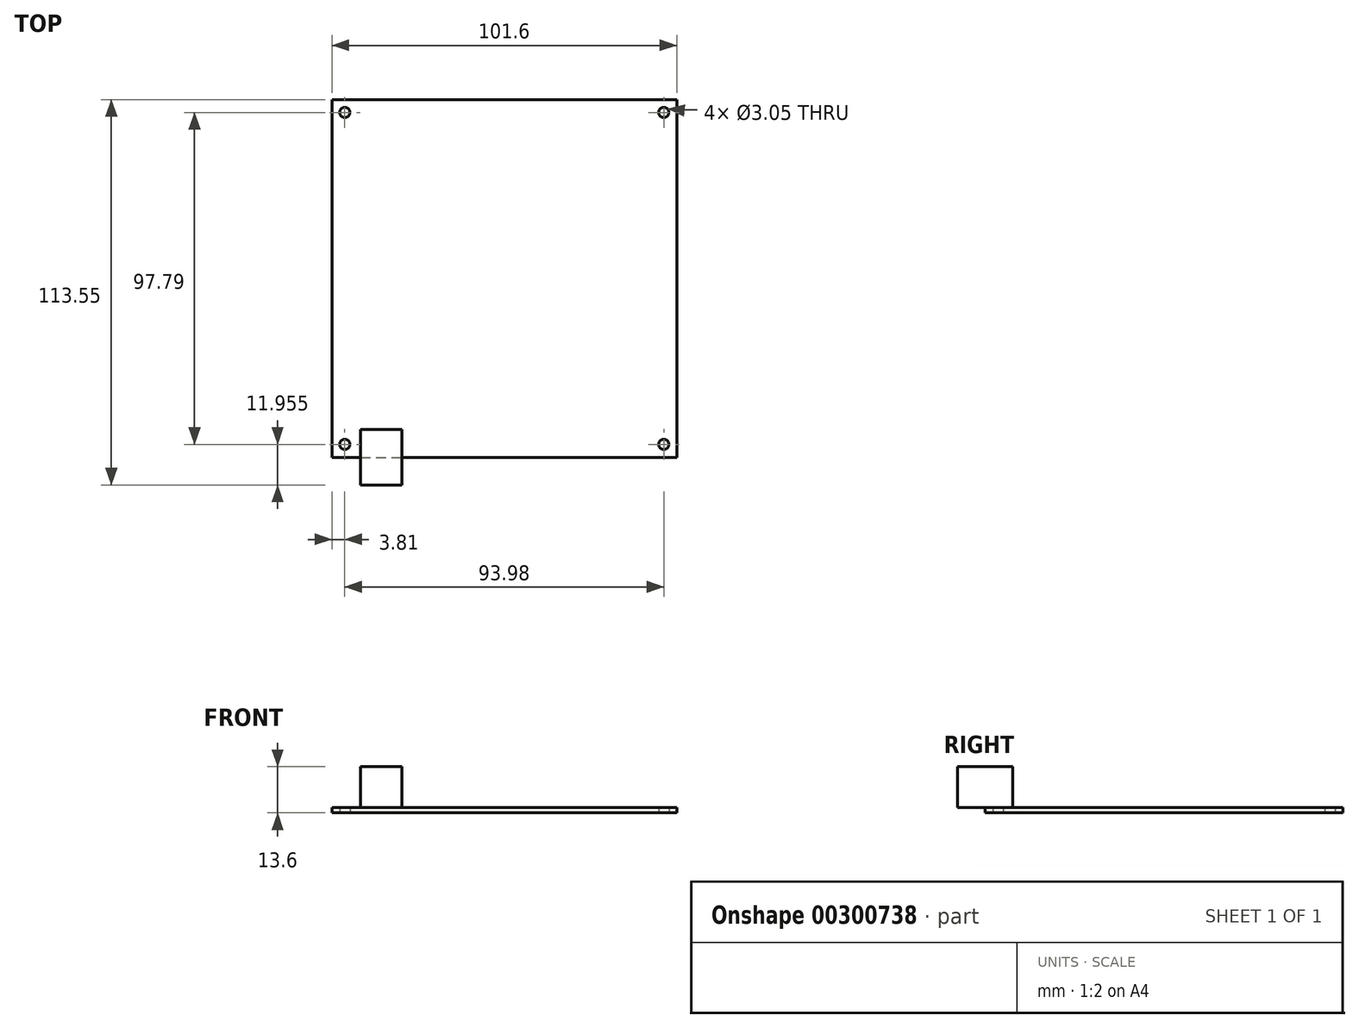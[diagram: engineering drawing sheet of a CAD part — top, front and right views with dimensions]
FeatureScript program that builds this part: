
annotation { "Feature Type Name" : "Feature", "Feature Type Description" : "" }
export const myFeature = defineFeature(function(context is Context, id is Id, definition is map)
    precondition{}
    {
        {
            var Q0;
            Q0=qCreatedBy(makeId("Top.planeOp"),FACE);
            var sketch = newSketch(context, id + "F0", { "sketchPlane" : qUnion([Q0])});
            skLineSegment(sketch, "E0.bottom", {"start": v(-50.8, 52.7) * mm, "end": v(50.8, 52.7) * mm});
            skLineSegment(sketch, "E0.top", {"start": v(-50.8, -52.7) * mm, "end": v(50.8, -52.7) * mm});
            skLineSegment(sketch, "E0.left", {"start": v(-50.8, 52.7) * mm, "end": v(-50.8, -52.7) * mm});
            skLineSegment(sketch, "E0.right", {"start": v(50.8, 52.7) * mm, "end": v(50.8, -52.7) * mm});
            skPoint(sketch, "E0.middle", {"position": v(0, 0) * mm});
            skCircle(sketch, "E1", {"center": v(-46.99, 48.9) * mm, "radius": 1.52 * mm});
            skCircle(sketch, "E2", {"center": v(47, 48.9) * mm, "radius": 1.52 * mm});
            skCircle(sketch, "E3", {"center": v(46.99, -48.9) * mm, "radius": 1.52 * mm});
            skCircle(sketch, "E4", {"center": v(-47, -48.9) * mm, "radius": 1.52 * mm});
            skPoint(sketch, "E5.middle", {"position": v(-36.32, -52.7) * mm});
            skSolve(sketch);
        }
        {
            var Q0;
            Q0=makeQuery(id+"F0.imprint","IMPRINT",FACE,{"disambiguationData":[TD([[makeQuery(id+"F0.imprint","IMPRINT",EDGE,{"derivedFrom":sQuery(id+"F0.wireOp",EDGE,"E0.bottom")}),-1.0]])]});
            extrude(context, id + "F1", {"entities" : qUnion([Q0]), "depth" : 1.6 * mm});
        }
        {
            var Q0;
            Q0=makeQuery(id+"F1.opExtrude","CAP_FACE",FACE,{"disambiguationData":[OSD([sQuery(id+"F0.wireOp",EDGE,"E0.bottom"),sQuery(id+"F0.wireOp",EDGE,"E0.top"),sQuery(id+"F0.wireOp",EDGE,"E0.left"),sQuery(id+"F0.wireOp",EDGE,"E0.right"),sQuery(id+"F0.wireOp",EDGE,"E1"),sQuery(id+"F0.wireOp",EDGE,"E2"),sQuery(id+"F0.wireOp",EDGE,"E3"),sQuery(id+"F0.wireOp",EDGE,"E4")])],"isStart":false});
            var sketch = newSketch(context, id + "F2", { "sketchPlane" : qUnion([Q0])});
            skLineSegment(sketch, "E6.bottom", {"start": v(-30.22, -60.86) * mm, "end": v(-42.42, -60.86) * mm});
            skLineSegment(sketch, "E6.top", {"start": v(-30.22, -44.56) * mm, "end": v(-42.42, -44.56) * mm});
            skLineSegment(sketch, "E6.left", {"start": v(-30.22, -60.86) * mm, "end": v(-30.22, -44.56) * mm});
            skLineSegment(sketch, "E6.right", {"start": v(-42.42, -60.86) * mm, "end": v(-42.42, -44.55) * mm});
            skPoint(sketch, "E6.middle", {"position": v(-36.32, -52.7) * mm});
            skSolve(sketch);
        }
        {
            var Q0;
            Q0 = qSketchRegion(id + "F2", true);
            extrude(context, id + "F3", {"entities" : qUnion([Q0]), "depth" : 12 * mm});
        }
    });
